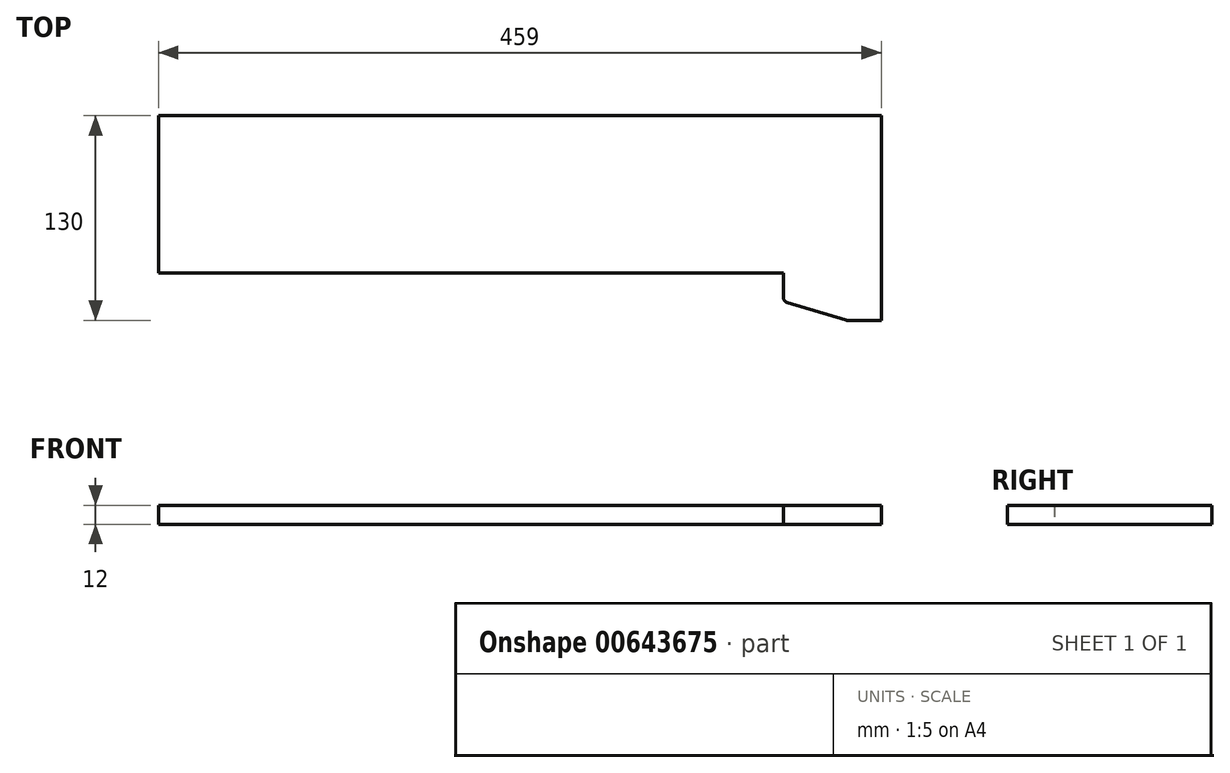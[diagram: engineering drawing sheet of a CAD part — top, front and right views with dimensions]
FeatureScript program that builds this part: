
annotation { "Feature Type Name" : "Feature", "Feature Type Description" : "" }
export const myFeature = defineFeature(function(context is Context, id is Id, definition is map)
    precondition{}
    {
        {
            var Q0;
            Q0=qCreatedBy(makeId("Top.planeOp"),FACE);
            var sketch = newSketch(context, id + "F0", { "sketchPlane" : qUnion([Q0])});
            skLineSegment(sketch, "E0.bottom", {"start": v(229.5, 0) * mm, "end": v(207.5, 0) * mm});
            skLineSegment(sketch, "E0.top", {"start": v(229.5, 130) * mm, "end": v(-229.5, 130) * mm});
            skLineSegment(sketch, "E0.left", {"start": v(229.5, 0) * mm, "end": v(229.5, 130) * mm});
            skLineSegment(sketch, "E0.right", {"start": v(-229.5, 30) * mm, "end": v(-229.5, 130) * mm});
            skPoint(sketch, "E0.middle", {"position": v(0, 65) * mm});
            skLineSegment(sketch, "E1", {"start": v(-229.5, 30) * mm, "end": v(167.5, 30) * mm});
            skLineSegment(sketch, "E2", {"start": v(167.5, 30) * mm, "end": v(167.5, 12) * mm});
            skLineSegment(sketch, "E3", {"start": v(167.5, 12) * mm, "end": v(207.5, 0) * mm});
            skPoint(sketch, "E4.orphan", {"position": v(-229.5, 0) * mm});
            skSolve(sketch);
        }
        {
            var Q0;
            Q0 = qSketchRegion(id + "F0", true);
            extrude(context, id + "F1", {"entities" : qUnion([Q0]), "depth" : 12 * mm, "offsetDistance" : 25 * mm});
        }
        {
            var Q0;
            Q0=makeQuery(id+"F1.opExtrude","SWEPT_EDGE",EDGE,{"disambiguationData":[OSD([sQuery(id+"F0.wireOp",EDGE,"E0.bottom"),sQuery(id+"F0.wireOp",EDGE,"E3")])]});
            var Q1;
            Q1=makeQuery(id+"F1.opExtrude","SWEPT_EDGE",EDGE,{"disambiguationData":[OSD([sQuery(id+"F0.wireOp",EDGE,"E2"),sQuery(id+"F0.wireOp",EDGE,"E3")])]});
            fillet(context, id + "F2", {"entities" : qUnion([Q0, Q1]), "radius" : 3 * mm, "tangentPropagation" : true, "allowEdgeOverflow" : false});
        }
    });
